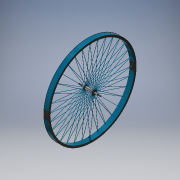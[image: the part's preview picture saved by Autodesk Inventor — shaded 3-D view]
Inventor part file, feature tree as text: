
AUTODESK INVENTOR PART (.ipt)
format: ipt  version: 2018 (Build 220112000, 112)  size: 1,147,904 bytes
history: native  units: mm
features: sketch x9, extrude x5, fillet x4, mirror x3, thread x2, plane x2, revolve x1, sweep x1, pattern_circular x1
ambient origin geometry x8: Origin, YZ Plane, XZ Plane, XY Plane, X Axis, Y Axis, Z Axis, Center Point
bodies: Solid1 (feature_tree)
feature tree (28):
  revolve  "Revolution1"  [1 undecoded]
  extrude  "Extrusion1"  Depth=8.0mm
  extrude  "Extrusion2"  TaperAngle=90.0deg  [1 undecoded]
  mirror  "Mirror1"
  fillet  "Fillet1"  Radius=15.0mm
  fillet  "Fillet2"  Radius=48.5mm
  extrude  "Extrusion3"  Depth=2.0mm TaperAngle=0.0deg
  extrude  "Extrusion4"  Depth=2.0mm
  extrude  "Extrusion5"  Depth=10.0mm TaperAngle=0.0deg
  thread  "Thread1"  [1 undecoded]
  mirror  "Mirror2"
  thread  "Thread2"  [1 undecoded]
  fillet  "Fillet3"  Radius=7.0mm
  fillet  "Fillet4"  Radius=18.0mm
  plane  "Work Plane1"
  sketch  "Sketch7"  dims[d34=10.0mm d35=0.0mm d36=10.0mm d37=0.0mm]
  plane  "Work Plane2"
  sweep  "Sweep1"
  pattern_circular  "Circular Pattern1"  [2 undecoded]
  mirror  "Mirror3"
  sketch  "Sketch1"  dims[d8=12.5mm d9=2.0mm]
  sketch  "Sketch2"  dims[d10=2.0mm d11=8.0mm]
  sketch  "Sketch3"  dims[d15=2.0mm d16=90.0deg d17=15.0mm d18=48.5mm d19=0.0mm]
  sketch  "Sketch4"  dims[d20=30.0mm d21=2.0mm d22=0.0mm]
  sketch  "Sketch5"  dims[d23=2.0mm d24=2.0mm]
  sketch  "Sketch6"  dims[d25=7.0mm d26=19.75mm d27=0.0mm d28=10.0mm d29=2.0mm d30=0.0mm d31=7.0mm d32=18.0mm d33=0.0mm]
  sketch  "Sketch8"  dims[d38=2.0mm d39=2.0mm d40=250.0mm d41=-251.0mm d42=12.5mm d43=-15.0mm d44=2.0mm d45=2.0mm d46=0.0mm d47=320.0mm d48=360.0deg d50=0.0mm]
  sketch  "3D Sketch1"
note: 6 required parameter values undecoded (feature->parameter linkage not recoverable at this tier; creation-order binding heuristic only, values carry confidence <= 0.55)